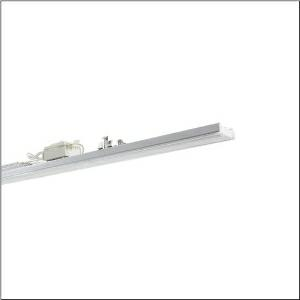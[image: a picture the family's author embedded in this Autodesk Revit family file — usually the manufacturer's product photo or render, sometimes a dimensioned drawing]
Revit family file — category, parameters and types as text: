
# Revit family: licross_r__11_recessed_mo_51tl1edv4e5g_e8d9
name_source: partatom
category: Lighting Fixtures
units: mm (PartAtom-declared; Revit-internal decimal feet)

## family parameters
Cut with Voids When Loaded = No
Host = Face
Light Source = No
Part Type = Normal
Room Calculation Point = No
Round Connector Dimension = Use Diameter
Shared = No

## types (1)
- --- (1 x LED, 14850 lm, 84.1 W, 4000K)
    Apparent Load = 84 VA
    CIE Flux Codes = 85 95 99 100 100
    Color Rendering = 80
    Color Temperature = 4000K
    Default Elevation = 1800 mm
    Description = Licross® 11 Recessed MO, luminaire insert, of sheet steel, coil coated, white, length: 2.250mm, width: 66mm, height: 67mm, LED rated luminous flux: 14.850lm, light colour: 840, control gear: DALI 2, with plug, 5-pole, with phase selection, mains connection: 220..240V, AC, 50/60Hz, rated input power: 84W, internal wiring halogen-free, primary light control with lens, of plastic, primary optical cover: cover, of PMMA, light emission: direct distribution, primary light characteristic: symmetric, protection rating (complete): IP40, insulation class (complete): insulation class I (protective earthing), certification: CE, ENEC, VDE, UKCA, protection symbol: D if used in an environment without relevant dust loads with corresponding accessories, impact resistance: IK06, permissible ambient temperature for indoor applications: -25..+35°C, corresponds to IFS (International Featured Standards) requirements for safety and quality in the food industry, reducing of maximum allowable ambient temperature of 5°C with ceiling mounting, LABS conformity tested according to VDMA 24364:2018-05, packaging unit: 1 piece
    Height = 58 mm
    Lamp = 1 x LED
    Lamp Light Flux = 14850 lm
    Lamp Power = 84.1 W
    Lamp count = 1
    Length = 2250 mm
    Luminous efficacy = 177 lm/W
    Manufacturer = Siteco
    ModVariant = No
    Model = 51TL1EDV4E5G
    Mounting Place = Ceiling
    Mounting Type = Pendant
    Number of Poles = 1
    OnlyDefault = Yes
    Power Factor = 1
    Product Name = Licross® 11 Recessed MO
    Product group = luminaire insert | ceiling pendant
    ProductGroupID = 902
    Protection Class = Protection class I
    Protection Degree = IP 40
    RLX_Detail_Level = 1
    RLX_Emergency_Light_Flux = 0 lm
    RLX_Emergency_Type = 0
    RLX_Emergency_Type_DB = No
    RlxData = <blob elided: 29589 chars, md5=ffcd800d>
    Socket = socket
    Standby Power = 0 W
    System Light Flux = 14850 lm
    System Power = 84 W
    Type Comments = factory setting: luminous flux: 100 % | dim-lin: 254 | 378 mA
    Type Image = l_1296930.jpg
    URL = http://relux.com
    VarID = @adj_117395
    Voltage = 0 V
    Weight = 0.00 kg
    Width = 66 mm

## geometry (parser evidence)
native form markers: Blend x4, Sweep x9
no freeform markers — native parametric forms only
